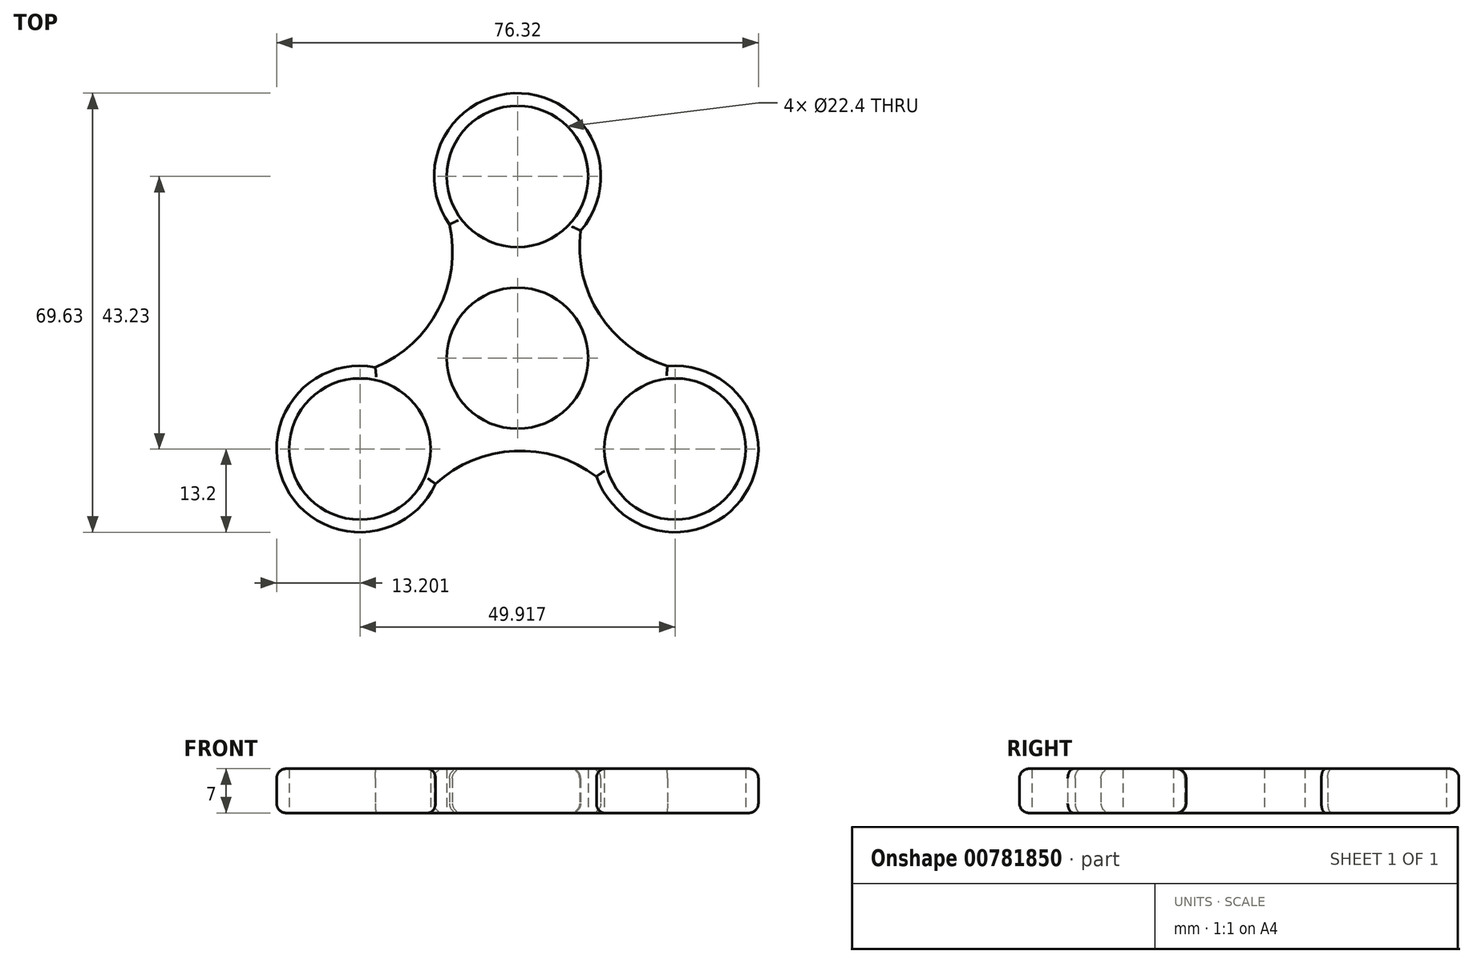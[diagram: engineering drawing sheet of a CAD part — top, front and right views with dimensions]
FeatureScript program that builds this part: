
annotation { "Feature Type Name" : "Feature", "Feature Type Description" : "" }
export const myFeature = defineFeature(function(context is Context, id is Id, definition is map)
    precondition{}
    {
        {
            var Q0;
            Q0=qCreatedBy(makeId("Top.planeOp"),FACE);
            var sketch = newSketch(context, id + "F0", { "sketchPlane" : qUnion([Q0])});
            skCircle(sketch, "E0", {"center": v(0, 0) * mm, "radius": 11.2 * mm});
            skCircle(sketch, "E1", {"center": v(0, 28.82) * mm, "radius": 11.2 * mm});
            skArc(sketch, "E2", {"start": v(10.02, 20.22) * mm, "mid": v(0.63, 42) * mm, "end": v(-10.8, 21.22) * mm});
            skArc(sketch, "E3.1.0", {"start": v(-22.52, -1.44) * mm, "mid": v(-36.7, -20.46) * mm, "end": v(-12.98, -19.95) * mm});
            skCircle(sketch, "E3.1.1", {"center": v(-24.96, -14.4) * mm, "radius": 11.2 * mm});
            skArc(sketch, "E3.2.0", {"start": v(12.5, -18.78) * mm, "mid": v(36.06, -21.55) * mm, "end": v(23.77, -1.26) * mm});
            skCircle(sketch, "E3.2.1", {"center": v(24.96, -14.4) * mm, "radius": 11.2 * mm});
            skArc(sketch, "E4", {"start": v(10.02, 20.22) * mm, "mid": v(12.98, 6.97) * mm, "end": v(23.77, -1.26) * mm});
            skArc(sketch, "E5.1.0", {"start": v(-22.52, -1.44) * mm, "mid": v(-12.53, 7.75) * mm, "end": v(-10.8, 21.22) * mm});
            skArc(sketch, "E5.2.0", {"start": v(12.5, -18.78) * mm, "mid": v(-0.45, -14.72) * mm, "end": v(-12.98, -19.95) * mm});
            skSolve(sketch);
        }
        {
            var Q0;
            Q0=qSketchRegion(id+"F0",true);
            extrude(context, id + "F1", {"entities" : qUnion([Q0]), "depth" : 7 * mm, "offsetDistance" : 25 * mm});
        }
        {
            var Q0;
            Q0=makeQuery(id+"F1.opExtrude","CAP_EDGE",EDGE,{"disambiguationData":[OSD([sQuery(id+"F0.wireOp",EDGE,"E2")])],"isStart":false});
            var Q1;
            Q1=makeQuery(id+"F1.opExtrude","CAP_EDGE",EDGE,{"disambiguationData":[OSD([sQuery(id+"F0.wireOp",EDGE,"E5.1.0")])],"isStart":false});
            var Q2;
            Q2=makeQuery(id+"F1.opExtrude","CAP_EDGE",EDGE,{"disambiguationData":[OSD([sQuery(id+"F0.wireOp",EDGE,"E4")])],"isStart":false});
            var Q3;
            Q3=makeQuery(id+"F1.opExtrude","CAP_EDGE",EDGE,{"disambiguationData":[OSD([sQuery(id+"F0.wireOp",EDGE,"E3.2.0")])],"isStart":false});
            var Q4;
            Q4=makeQuery(id+"F1.opExtrude","CAP_EDGE",EDGE,{"disambiguationData":[OSD([sQuery(id+"F0.wireOp",EDGE,"E5.2.0")])],"isStart":false});
            var Q5;
            Q5=makeQuery(id+"F1.opExtrude","CAP_EDGE",EDGE,{"disambiguationData":[OSD([sQuery(id+"F0.wireOp",EDGE,"E3.1.0")])],"isStart":false});
            fillet(context, id + "F2", {"entities" : qUnion([Q0, Q1, Q2, Q3, Q4, Q5]), "radius" : 1.5 * mm, "tangentPropagation" : true, "allowEdgeOverflow" : false});
        }
        {
            var Q0;
            Q0=makeQuery(id+"F1.opExtrude","CAP_EDGE",EDGE,{"disambiguationData":[OSD([sQuery(id+"F0.wireOp",EDGE,"E3.1.0")])],"isStart":true});
            var Q1;
            Q1=makeQuery(id+"F1.opExtrude","CAP_EDGE",EDGE,{"disambiguationData":[OSD([sQuery(id+"F0.wireOp",EDGE,"E5.2.0")])],"isStart":true});
            var Q2;
            Q2=makeQuery(id+"F1.opExtrude","CAP_EDGE",EDGE,{"disambiguationData":[OSD([sQuery(id+"F0.wireOp",EDGE,"E5.1.0")])],"isStart":true});
            var Q3;
            Q3=makeQuery(id+"F1.opExtrude","CAP_EDGE",EDGE,{"disambiguationData":[OSD([sQuery(id+"F0.wireOp",EDGE,"E2")])],"isStart":true});
            var Q4;
            Q4=makeQuery(id+"F1.opExtrude","CAP_EDGE",EDGE,{"disambiguationData":[OSD([sQuery(id+"F0.wireOp",EDGE,"E4")])],"isStart":true});
            var Q5;
            Q5=makeQuery(id+"F1.opExtrude","CAP_EDGE",EDGE,{"disambiguationData":[OSD([sQuery(id+"F0.wireOp",EDGE,"E3.2.0")])],"isStart":true});
            fillet(context, id + "F3", {"entities" : qUnion([Q0, Q1, Q2, Q3, Q4, Q5]), "radius" : 1.5 * mm, "tangentPropagation" : true, "allowEdgeOverflow" : false});
        }
    });
